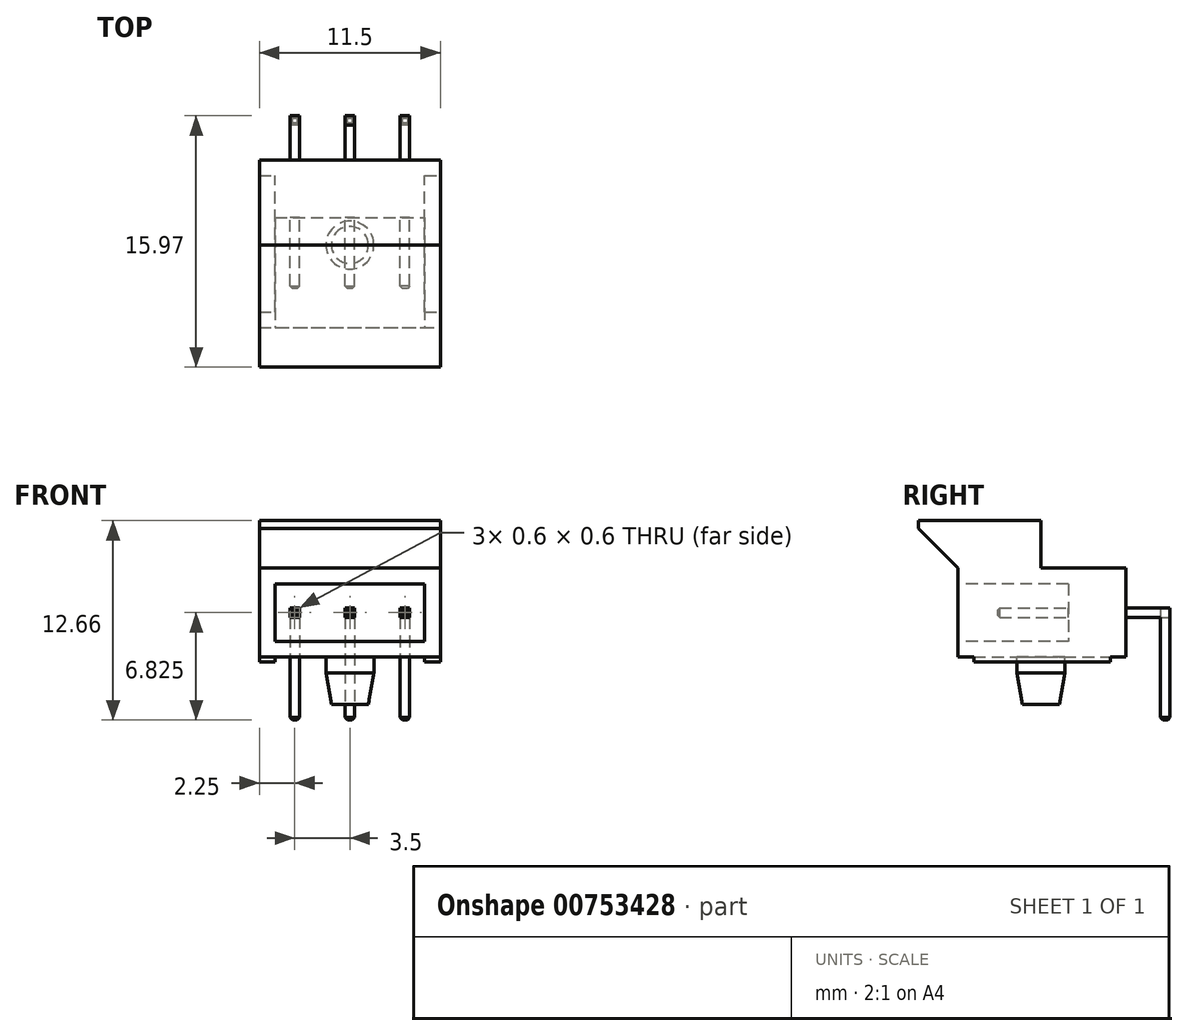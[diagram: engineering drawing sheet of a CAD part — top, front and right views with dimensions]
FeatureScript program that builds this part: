
annotation { "Feature Type Name" : "Feature", "Feature Type Description" : "" }
export const myFeature = defineFeature(function(context is Context, id is Id, definition is map)
    precondition{}
    {
        {
            var Q0;
            Q0=qCreatedBy(makeId("Top.planeOp"),FACE);
            var sketch = newSketch(context, id + "F0", { "sketchPlane" : qUnion([Q0])});
            skLineSegment(sketch, "E0.bottom", {"start": v(-5.75, 7.83) * mm, "end": v(5.75, 7.83) * mm});
            skLineSegment(sketch, "E0.top", {"start": v(-5.75, -7.83) * mm, "end": v(5.75, -7.83) * mm});
            skLineSegment(sketch, "E0.left", {"start": v(-5.75, 7.83) * mm, "end": v(-5.75, -7.83) * mm});
            skLineSegment(sketch, "E0.right", {"start": v(5.75, 7.83) * mm, "end": v(5.75, -7.83) * mm});
            skCircle(sketch, "E1", {"center": v(0, -2.58) * mm, "radius": 1.52 * mm});
            skCircle(sketch, "E2", {"center": v(-3.5, 5.33) * mm, "radius": 0.51 * mm});
            skCircle(sketch, "E3", {"center": v(0, 5.33) * mm, "radius": 0.51 * mm});
            skCircle(sketch, "E4", {"center": v(3.5, 5.33) * mm, "radius": 0.51 * mm});
            skLineSegment(sketch, "E5", {"start": v(-5.75, 2.83) * mm, "end": v(5.75, 2.83) * mm});
            skSolve(sketch);
        }
        {
            var Q0;
            {var subQ1=sQuery(id+"F0.wireOp",EDGE,"E0.top");Q0=makeQuery(id+"F0.imprint","IMPRINT",FACE,{"disambiguationData":[TD([[makeQuery(id+"F0.imprint","IMPRINT",EDGE,{"derivedFrom":subQ1}),1.0]])]});}
            var Q1;
            Q1=makeQuery(id+"F0.imprint","IMPRINT",FACE,{"disambiguationData":[TD([[makeQuery(id+"F0.imprint","IMPRINT",EDGE,{"derivedFrom":sQuery(id+"F0.wireOp",EDGE,"E1")}),1.0]])]});
            extrude(context, id + "F1", {"entities" : qUnion([Q0, Q1]), "depth" : 5.65 * mm, "offsetDistance" : 25 * mm});
        }
        {
            var Q0;
            Q0=makeQuery(id+"F0.imprint","IMPRINT",FACE,{"disambiguationData":[TD([[makeQuery(id+"F0.imprint","IMPRINT",EDGE,{"derivedFrom":sQuery(id+"F0.wireOp",EDGE,"E1")}),1.0]])]});
            extrude(context, id + "F2", {"entities" : qUnion([Q0]), "operationType" : NewBodyOperationType.ADD, "oppositeDirection" : true, "depth" : 3 * mm, "offsetDistance" : 25 * mm});
        }
        {
            var Q0;
            Q0=makeQuery(id+"F2.opExtrude","CAP_EDGE",EDGE,{"disambiguationData":[OSD([sQuery(id+"F0.wireOp",EDGE,"E1")])],"isStart":false});
            chamfer(context, id + "F3", {"entities" : qUnion([Q0]), "chamferType" : ChamferType.OFFSET_ANGLE, "width" : 2 * mm, "oppositeDirection" : false, "angle" : 10 * degree, "tangentPropagation" : true});
        }
        {
            var Q0;
            Q0=makeQuery(id+"F1.opExtrude","SWEPT_FACE",FACE,{"disambiguationData":[OSD([sQuery(id+"F0.wireOp",EDGE,"E0.top")])]});
            var sketch = newSketch(context, id + "F4", { "sketchPlane" : qUnion([Q0])});
            skLineSegment(sketch, "E6.bottom", {"start": v(-4.75, 4.65) * mm, "end": v(4.75, 4.65) * mm});
            skLineSegment(sketch, "E6.top", {"start": v(-4.75, 1) * mm, "end": v(4.75, 1) * mm});
            skLineSegment(sketch, "E6.left", {"start": v(-4.75, 4.65) * mm, "end": v(-4.75, 1) * mm});
            skLineSegment(sketch, "E6.right", {"start": v(4.75, 4.65) * mm, "end": v(4.75, 1) * mm});
            skSolve(sketch);
        }
        {
            var Q0;
            Q0=makeQuery(id+"F4.imprint","IMPRINT",FACE,{"disambiguationData":[TD([[makeQuery(id+"F4.imprint","IMPRINT",EDGE,{"derivedFrom":sQuery(id+"F4.wireOp",EDGE,"E6.bottom")}),-1.0]])]});
            extrude(context, id + "F5", {"entities" : qUnion([Q0]), "operationType" : NewBodyOperationType.REMOVE, "oppositeDirection" : true, "depth" : 7 * mm, "offsetDistance" : 25 * mm});
        }
        {
            var Q0;
            Q0=makeQuery(id+"F1.opExtrude","SWEPT_FACE",FACE,{"disambiguationData":[OSD([sQuery(id+"F0.wireOp",EDGE,"E0.right")])]});
            var Q1;
            Q1=makeQuery(id+"F1.opExtrude","SWEPT_FACE",FACE,{"disambiguationData":[OSD([sQuery(id+"F0.wireOp",EDGE,"E0.left")])]});
            cPlane(context, id + "F6", {"entities" : qUnion([Q0, Q1]), "cplaneType" : CPlaneType.MID_PLANE, "offset" : 25 * mm, "width" : 150 * mm, "height" : 150 * mm});
        }
        {
            var Q0;
            Q0=qCreatedBy(id+"F6.planeOp",FACE);
            var sketch = newSketch(context, id + "F7", { "sketchPlane" : qUnion([Q0])});
            skLineSegment(sketch, "E7.bottom", {"start": v(-5.33, 3.12) * mm, "end": v(5.63, 3.12) * mm});
            skLineSegment(sketch, "E7.top", {"start": v(-5.33, 2.53) * mm, "end": v(5.63, 2.53) * mm});
            skLineSegment(sketch, "E7.left", {"start": v(-5.33, 3.12) * mm, "end": v(-5.33, 2.53) * mm});
            skLineSegment(sketch, "E7.right", {"start": v(5.63, 3.12) * mm, "end": v(5.63, 2.53) * mm});
            skLineSegment(sketch, "E8.bottom", {"start": v(5.63, 3.12) * mm, "end": v(5.03, 3.12) * mm});
            skLineSegment(sketch, "E8.top", {"start": v(5.63, -4) * mm, "end": v(5.03, -4) * mm});
            skLineSegment(sketch, "E8.left", {"start": v(5.63, 3.12) * mm, "end": v(5.63, -4) * mm});
            skLineSegment(sketch, "E8.right", {"start": v(5.03, 3.12) * mm, "end": v(5.03, -4) * mm});
            skLineSegment(sketch, "E9.0", {"start": v(4.82, 0) * mm, "end": v(5.84, 0) * mm});
            skLineSegment(sketch, "E10.0.0", {"start": v(-7.83, 4.65) * mm, "end": v(-7.83, 1) * mm});
            skLineSegment(sketch, "E10.0.1", {"start": v(-7.83, 1) * mm, "end": v(-0.83, 1) * mm});
            skLineSegment(sketch, "E10.0.2", {"start": v(-0.83, 1) * mm, "end": v(-0.83, 4.65) * mm});
            skLineSegment(sketch, "E10.0.3", {"start": v(-0.83, 4.65) * mm, "end": v(-7.83, 4.65) * mm});
            skLineSegment(sketch, "E11", {"start": v(-5.33, 2.83) * mm, "end": v(5.63, 2.83) * mm, "construction": true});
            skLineSegment(sketch, "E12", {"start": v(5.33, 3.12) * mm, "end": v(5.33, -4) * mm, "construction": true});
            skSolve(sketch);
        }
        {
            var Q0;
            {var subQ0=sQuery(id+"F7.wireOp",EDGE,"E7.left");Q0=makeQuery(id+"F7.imprint","IMPRINT",FACE,{"disambiguationData":[TD([[makeQuery(id+"F7.imprint","IMPRINT",EDGE,{"derivedFrom":subQ0}),1.0]])]});}
            var Q1;
            {var subQ5=sQuery(id+"F7.wireOp",EDGE,"E8.bottom");Q1=makeQuery(id+"F7.imprint","IMPRINT",FACE,{"disambiguationData":[TD([[makeQuery(id+"F7.imprint","IMPRINT",EDGE,{"derivedFrom":subQ5}),1.0]])]});}
            var Q2;
            {var subQ0=sQuery(id+"F7.wireOp",EDGE,"E8.top");Q2=makeQuery(id+"F7.imprint","IMPRINT",FACE,{"disambiguationData":[TD([[makeQuery(id+"F7.imprint","IMPRINT",EDGE,{"derivedFrom":subQ0}),-1.0]])]});}
            var Q3;
            {var subQ5=sQuery(id+"F7.wireOp",EDGE,"E9.0");Q3=makeQuery(id+"F7.imprint","IMPRINT",FACE,{"disambiguationData":[TD([[makeQuery(id+"F7.imprint","IMPRINT",EDGE,{"derivedFrom":subQ5}),1.0]])]});}
            var Q4;
            {var subQ3=sQuery(id+"F7.wireOp",EDGE,"E10.0.2");var subQ5=sQuery(id+"F7.wireOp",EDGE,"E7.top");var subQ7=makeQuery(id+"F7.imprint","INTERSECT",VERTEX,{"derivedFrom":[subQ5,subQ3]});Q4=makeQuery(id+"F7.imprint","IMPRINT",FACE,{"disambiguationData":[TD([[makeQuery(id+"F7.imprint","IMPRINT",EDGE,{"disambiguationData":[TD([[subQ7,-1.0]])],"derivedFrom":subQ5}),1.0]])]});}
            extrude(context, id + "F8", {"entities" : qUnion([Q0, Q1, Q2, Q3, Q4]), "operationType" : NewBodyOperationType.ADD, "depth" : 0.3 * mm, "offsetDistance" : 25 * mm, "hasSecondDirection" : true, "secondDirectionOppositeDirection" : true, "secondDirectionDepth" : 0.3 * mm});
        }
        {
            var Q0;
            Q0=qCreatedBy(id+"F6.planeOp",FACE);
            cPlane(context, id + "F9", {"entities" : qUnion([Q0]), "cplaneType" : CPlaneType.OFFSET, "offset" : 3.5 * mm, "width" : 150 * mm, "height" : 150 * mm});
        }
        {
            var Q0;
            Q0=qCreatedBy(id+"F9.planeOp",FACE);
            var sketch = newSketch(context, id + "F10", { "sketchPlane" : qUnion([Q0])});
            skLineSegment(sketch, "E13.0", {"start": v(-5.33, 3.12) * mm, "end": v(5.63, 3.12) * mm});
            skLineSegment(sketch, "E14.0", {"start": v(-5.33, 2.53) * mm, "end": v(5.63, 2.53) * mm});
            skLineSegment(sketch, "E15.0", {"start": v(-5.33, 3.12) * mm, "end": v(-5.33, 2.53) * mm});
            skLineSegment(sketch, "E16.0", {"start": v(5.63, 3.12) * mm, "end": v(5.63, -4) * mm});
            skLineSegment(sketch, "E17.0", {"start": v(5.03, 3.12) * mm, "end": v(5.03, -4) * mm});
            skLineSegment(sketch, "E18.0", {"start": v(5.63, -4) * mm, "end": v(5.03, -4) * mm});
            skSolve(sketch);
        }
        {
            var Q0;
            {var subQ0=sQuery(id+"F10.wireOp",EDGE,"E15.0");Q0=makeQuery(id+"F10.imprint","IMPRINT",FACE,{"disambiguationData":[TD([[makeQuery(id+"F10.imprint","IMPRINT",EDGE,{"derivedFrom":subQ0}),1.0]])]});}
            var Q1;
            {var subQ0=sQuery(id+"F10.wireOp",EDGE,"E16.0");var subQ1=sQuery(id+"F10.wireOp",EDGE,"E13.0");var subQ2=makeQuery(id+"F10.imprint","INTERSECT",VERTEX,{"derivedFrom":[subQ1,subQ0]});Q1=makeQuery(id+"F10.imprint","IMPRINT",FACE,{"disambiguationData":[TD([[makeQuery(id+"F10.imprint","IMPRINT",EDGE,{"disambiguationData":[TD([[subQ2,1.0]])],"derivedFrom":subQ1}),-1.0]])]});}
            var Q2;
            {var subQ5=sQuery(id+"F10.wireOp",EDGE,"E18.0");Q2=makeQuery(id+"F10.imprint","IMPRINT",FACE,{"disambiguationData":[TD([[makeQuery(id+"F10.imprint","IMPRINT",EDGE,{"derivedFrom":subQ5}),-1.0]])]});}
            extrude(context, id + "F11", {"entities" : qUnion([Q0, Q1, Q2]), "operationType" : NewBodyOperationType.ADD, "depth" : 0.3 * mm, "offsetDistance" : 25 * mm, "hasSecondDirection" : true, "secondDirectionOppositeDirection" : true, "secondDirectionDepth" : 0.3 * mm});
        }
        {
            var Q0;
            Q0=qCreatedBy(id+"F6.planeOp",FACE);
            cPlane(context, id + "F12", {"entities" : qUnion([Q0]), "cplaneType" : CPlaneType.OFFSET, "offset" : 3.5 * mm, "oppositeDirection" : true, "width" : 150 * mm, "height" : 150 * mm});
        }
        {
            var Q0;
            Q0=qCreatedBy(id+"F12.planeOp",FACE);
            var sketch = newSketch(context, id + "F13", { "sketchPlane" : qUnion([Q0])});
            skLineSegment(sketch, "E19.0", {"start": v(-5.33, 3.12) * mm, "end": v(5.63, 3.12) * mm});
            skLineSegment(sketch, "E20.0", {"start": v(5.63, 3.12) * mm, "end": v(5.63, -4) * mm});
            skLineSegment(sketch, "E21.0", {"start": v(5.63, -4) * mm, "end": v(5.03, -4) * mm});
            skLineSegment(sketch, "E22.0", {"start": v(5.03, 3.12) * mm, "end": v(5.03, -4) * mm});
            skLineSegment(sketch, "E23.0", {"start": v(-5.33, 2.53) * mm, "end": v(5.63, 2.53) * mm});
            skLineSegment(sketch, "E24.0", {"start": v(-5.33, 3.12) * mm, "end": v(-5.33, 2.53) * mm});
            skSolve(sketch);
        }
        {
            var Q0;
            {var subQ0=sQuery(id+"F13.wireOp",EDGE,"E24.0");Q0=makeQuery(id+"F13.imprint","IMPRINT",FACE,{"disambiguationData":[TD([[makeQuery(id+"F13.imprint","IMPRINT",EDGE,{"derivedFrom":subQ0}),1.0]])]});}
            var Q1;
            {var subQ0=sQuery(id+"F13.wireOp",EDGE,"E20.0");var subQ1=sQuery(id+"F13.wireOp",EDGE,"E19.0");var subQ2=makeQuery(id+"F13.imprint","INTERSECT",VERTEX,{"derivedFrom":[subQ1,subQ0]});Q1=makeQuery(id+"F13.imprint","IMPRINT",FACE,{"disambiguationData":[TD([[makeQuery(id+"F13.imprint","IMPRINT",EDGE,{"disambiguationData":[TD([[subQ2,1.0]])],"derivedFrom":subQ1}),-1.0]])]});}
            var Q2;
            {var subQ0=sQuery(id+"F13.wireOp",EDGE,"E21.0");Q2=makeQuery(id+"F13.imprint","IMPRINT",FACE,{"disambiguationData":[TD([[makeQuery(id+"F13.imprint","IMPRINT",EDGE,{"derivedFrom":subQ0}),-1.0]])]});}
            extrude(context, id + "F14", {"entities" : qUnion([Q0, Q1, Q2]), "operationType" : NewBodyOperationType.ADD, "depth" : 0.3 * mm, "offsetDistance" : 25 * mm, "hasSecondDirection" : true, "secondDirectionOppositeDirection" : true, "secondDirectionDepth" : 0.3 * mm});
        }
        {
            var Q0;
            Q0=makeQuery(id+"F14.opExtrude","SWEPT_EDGE",EDGE,{"disambiguationData":[OSD([sQuery(id+"F13.wireOp",EDGE,"E21.0"),sQuery(id+"F13.wireOp",EDGE,"E22.0")])]});
            var Q1;
            Q1=makeQuery(id+"F14.opExtrude","CAP_EDGE",EDGE,{"disambiguationData":[OSD([sQuery(id+"F13.wireOp",EDGE,"E21.0")])],"isStart":true});
            var Q2;
            Q2=makeQuery(id+"F14.opExtrude","SWEPT_EDGE",EDGE,{"disambiguationData":[OSD([sQuery(id+"F13.wireOp",EDGE,"E20.0"),sQuery(id+"F13.wireOp",EDGE,"E21.0")])]});
            var Q3;
            Q3=makeQuery(id+"F14.opExtrude","CAP_EDGE",EDGE,{"disambiguationData":[OSD([sQuery(id+"F13.wireOp",EDGE,"E21.0")])],"isStart":false});
            var Q4;
            Q4=makeQuery(id+"F8.opExtrude","CAP_EDGE",EDGE,{"disambiguationData":[OSD([sQuery(id+"F7.wireOp",EDGE,"E8.top")])],"isStart":true});
            var Q5;
            Q5=makeQuery(id+"F8.opExtrude","SWEPT_EDGE",EDGE,{"disambiguationData":[OSD([sQuery(id+"F7.wireOp",EDGE,"E8.top"),sQuery(id+"F7.wireOp",EDGE,"E8.right")])]});
            var Q6;
            Q6=makeQuery(id+"F8.opExtrude","CAP_EDGE",EDGE,{"disambiguationData":[OSD([sQuery(id+"F7.wireOp",EDGE,"E8.top")])],"isStart":false});
            var Q7;
            Q7=makeQuery(id+"F8.opExtrude","SWEPT_EDGE",EDGE,{"disambiguationData":[OSD([sQuery(id+"F7.wireOp",EDGE,"E8.top"),sQuery(id+"F7.wireOp",EDGE,"E8.left")])]});
            var Q8;
            Q8=makeQuery(id+"F11.opExtrude","SWEPT_EDGE",EDGE,{"disambiguationData":[OSD([sQuery(id+"F10.wireOp",EDGE,"E17.0"),sQuery(id+"F10.wireOp",EDGE,"E18.0")])]});
            var Q9;
            Q9=makeQuery(id+"F11.opExtrude","CAP_EDGE",EDGE,{"disambiguationData":[OSD([sQuery(id+"F10.wireOp",EDGE,"E18.0")])],"isStart":true});
            var Q10;
            Q10=makeQuery(id+"F11.opExtrude","CAP_EDGE",EDGE,{"disambiguationData":[OSD([sQuery(id+"F10.wireOp",EDGE,"E18.0")])],"isStart":false});
            var Q11;
            Q11=makeQuery(id+"F11.opExtrude","SWEPT_EDGE",EDGE,{"disambiguationData":[OSD([sQuery(id+"F10.wireOp",EDGE,"E16.0"),sQuery(id+"F10.wireOp",EDGE,"E18.0")])]});
            var Q12;
            Q12=makeQuery(id+"F14.opExtrude","CAP_EDGE",EDGE,{"disambiguationData":[OSD([sQuery(id+"F13.wireOp",EDGE,"E24.0")])],"isStart":false});
            var Q13;
            Q13=makeQuery(id+"F14.opExtrude","SWEPT_EDGE",EDGE,{"disambiguationData":[OSD([sQuery(id+"F13.wireOp",EDGE,"E19.0"),sQuery(id+"F13.wireOp",EDGE,"E24.0")])]});
            var Q14;
            Q14=makeQuery(id+"F14.opExtrude","CAP_EDGE",EDGE,{"disambiguationData":[OSD([sQuery(id+"F13.wireOp",EDGE,"E24.0")])],"isStart":true});
            var Q15;
            Q15=makeQuery(id+"F14.opExtrude","SWEPT_EDGE",EDGE,{"disambiguationData":[OSD([sQuery(id+"F13.wireOp",EDGE,"E23.0"),sQuery(id+"F13.wireOp",EDGE,"E24.0")])]});
            var Q16;
            Q16=makeQuery(id+"F8.opExtrude","SWEPT_EDGE",EDGE,{"disambiguationData":[OSD([sQuery(id+"F7.wireOp",EDGE,"E7.bottom"),sQuery(id+"F7.wireOp",EDGE,"E7.left")])]});
            var Q17;
            Q17=makeQuery(id+"F8.opExtrude","CAP_EDGE",EDGE,{"disambiguationData":[OSD([sQuery(id+"F7.wireOp",EDGE,"E7.left")])],"isStart":true});
            var Q18;
            Q18=makeQuery(id+"F8.opExtrude","CAP_EDGE",EDGE,{"disambiguationData":[OSD([sQuery(id+"F7.wireOp",EDGE,"E7.left")])],"isStart":false});
            var Q19;
            Q19=makeQuery(id+"F8.opExtrude","SWEPT_EDGE",EDGE,{"disambiguationData":[OSD([sQuery(id+"F7.wireOp",EDGE,"E7.top"),sQuery(id+"F7.wireOp",EDGE,"E7.left")])]});
            var Q20;
            Q20=makeQuery(id+"F11.opExtrude","CAP_EDGE",EDGE,{"disambiguationData":[OSD([sQuery(id+"F10.wireOp",EDGE,"E15.0")])],"isStart":true});
            var Q21;
            Q21=makeQuery(id+"F11.opExtrude","SWEPT_EDGE",EDGE,{"disambiguationData":[OSD([sQuery(id+"F10.wireOp",EDGE,"E13.0"),sQuery(id+"F10.wireOp",EDGE,"E15.0")])]});
            var Q22;
            Q22=makeQuery(id+"F11.opExtrude","CAP_EDGE",EDGE,{"disambiguationData":[OSD([sQuery(id+"F10.wireOp",EDGE,"E15.0")])],"isStart":false});
            var Q23;
            Q23=makeQuery(id+"F11.opExtrude","SWEPT_EDGE",EDGE,{"disambiguationData":[OSD([sQuery(id+"F10.wireOp",EDGE,"E14.0"),sQuery(id+"F10.wireOp",EDGE,"E15.0")])]});
            chamfer(context, id + "F15", {"entities" : qUnion([Q0, Q1, Q2, Q3, Q4, Q5, Q6, Q7, Q8, Q9, Q10, Q11, Q12, Q13, Q14, Q15, Q16, Q17, Q18, Q19, Q20, Q21, Q22, Q23]), "width" : 0.15 * mm, "tangentPropagation" : true});
        }
        {
            var Q0;
            Q0=makeQuery(id+"F1.opExtrude","CAP_FACE",FACE,{"disambiguationData":[OSD([sQuery(id+"F0.wireOp",EDGE,"E0.top"),sQuery(id+"F0.wireOp",EDGE,"E0.left"),sQuery(id+"F0.wireOp",EDGE,"E0.right"),sQuery(id+"F0.wireOp",EDGE,"E5")])],"isStart":true});
            var sketch = newSketch(context, id + "F16", { "sketchPlane" : qUnion([Q0])});
            skLineSegment(sketch, "E25.bottom", {"start": v(-5.75, 6.83) * mm, "end": v(-4.75, 6.83) * mm});
            skLineSegment(sketch, "E25.top", {"start": v(-5.75, -1.83) * mm, "end": v(-4.75, -1.83) * mm});
            skLineSegment(sketch, "E25.left", {"start": v(-5.75, 6.83) * mm, "end": v(-5.75, -1.83) * mm});
            skLineSegment(sketch, "E25.right", {"start": v(-4.75, 6.83) * mm, "end": v(-4.75, -1.83) * mm});
            skLineSegment(sketch, "E26.bottom", {"start": v(4.75, 6.83) * mm, "end": v(5.75, 6.83) * mm});
            skLineSegment(sketch, "E26.top", {"start": v(4.75, -1.83) * mm, "end": v(5.75, -1.83) * mm});
            skLineSegment(sketch, "E26.left", {"start": v(4.75, 6.83) * mm, "end": v(4.75, -1.83) * mm});
            skLineSegment(sketch, "E26.right", {"start": v(5.75, 6.83) * mm, "end": v(5.75, -1.83) * mm});
            skSolve(sketch);
        }
        {
            var Q0;
            Q0=makeQuery(id+"F16.imprint","IMPRINT",FACE,{"disambiguationData":[TD([[makeQuery(id+"F16.imprint","IMPRINT",EDGE,{"derivedFrom":sQuery(id+"F16.wireOp",EDGE,"E26.bottom")}),-1.0]])]});
            var Q1;
            Q1=makeQuery(id+"F16.imprint","IMPRINT",FACE,{"disambiguationData":[TD([[makeQuery(id+"F16.imprint","IMPRINT",EDGE,{"derivedFrom":sQuery(id+"F16.wireOp",EDGE,"E25.bottom")}),-1.0]])]});
            extrude(context, id + "F17", {"entities" : qUnion([Q0, Q1]), "operationType" : NewBodyOperationType.ADD, "depth" : 0.3 * mm, "offsetDistance" : 25 * mm});
        }
        {
            var Q0;
            Q0=makeQuery(id+"F17.boolean.opBoolean","MERGE",FACE,{"derivedFrom":[makeQuery(id+"F1.opExtrude","SWEPT_FACE",FACE,{"disambiguationData":[OSD([sQuery(id+"F0.wireOp",EDGE,"E0.right")])]}),makeQuery(id+"F17.opExtrude","SWEPT_FACE",FACE,{"disambiguationData":[OSD([sQuery(id+"F16.wireOp",EDGE,"E26.right")])]})]});
            var sketch = newSketch(context, id + "F18", { "sketchPlane" : qUnion([Q0])});
            skLineSegment(sketch, "E27", {"start": v(-7.83, 5.65) * mm, "end": v(-10.84, 8.66) * mm});
            skLineSegment(sketch, "E28", {"start": v(-10.84, 8.66) * mm, "end": v(-2.58, 8.66) * mm});
            skLineSegment(sketch, "E29", {"start": v(-2.58, 8.66) * mm, "end": v(-2.58, 5.65) * mm});
            skLineSegment(sketch, "E30.0", {"start": v(-1.4, -3) * mm, "end": v(-3.75, -3) * mm});
            skLineSegment(sketch, "E31", {"start": v(-10.34, 8.16) * mm, "end": v(-10.34, 8.66) * mm});
            skSolve(sketch);
        }
        {
            var Q0;
            {var subQ0=sQuery(id+"F18.wireOp",EDGE,"E29");Q0=makeQuery(id+"F18.imprint","IMPRINT",FACE,{"disambiguationData":[TD([[makeQuery(id+"F18.imprint","IMPRINT",EDGE,{"derivedFrom":subQ0}),-1.0]])]});}
            var Q1;
            Q1=makeQuery(id+"F17.boolean.opBoolean","MERGE",FACE,{"derivedFrom":[makeQuery(id+"F1.opExtrude","SWEPT_FACE",FACE,{"disambiguationData":[OSD([sQuery(id+"F0.wireOp",EDGE,"E0.left")])]}),makeQuery(id+"F17.opExtrude","SWEPT_FACE",FACE,{"disambiguationData":[OSD([sQuery(id+"F16.wireOp",EDGE,"E25.left")])]})]});
            extrude(context, id + "F19", {"entities" : qUnion([Q0]), "operationType" : NewBodyOperationType.ADD, "endBound" : BoundingType.UP_TO_SURFACE, "oppositeDirection" : true, "depth" : 25 * mm, "endBoundEntityFace" : qUnion([Q1]), "offsetDistance" : 25 * mm});
        }
    });
